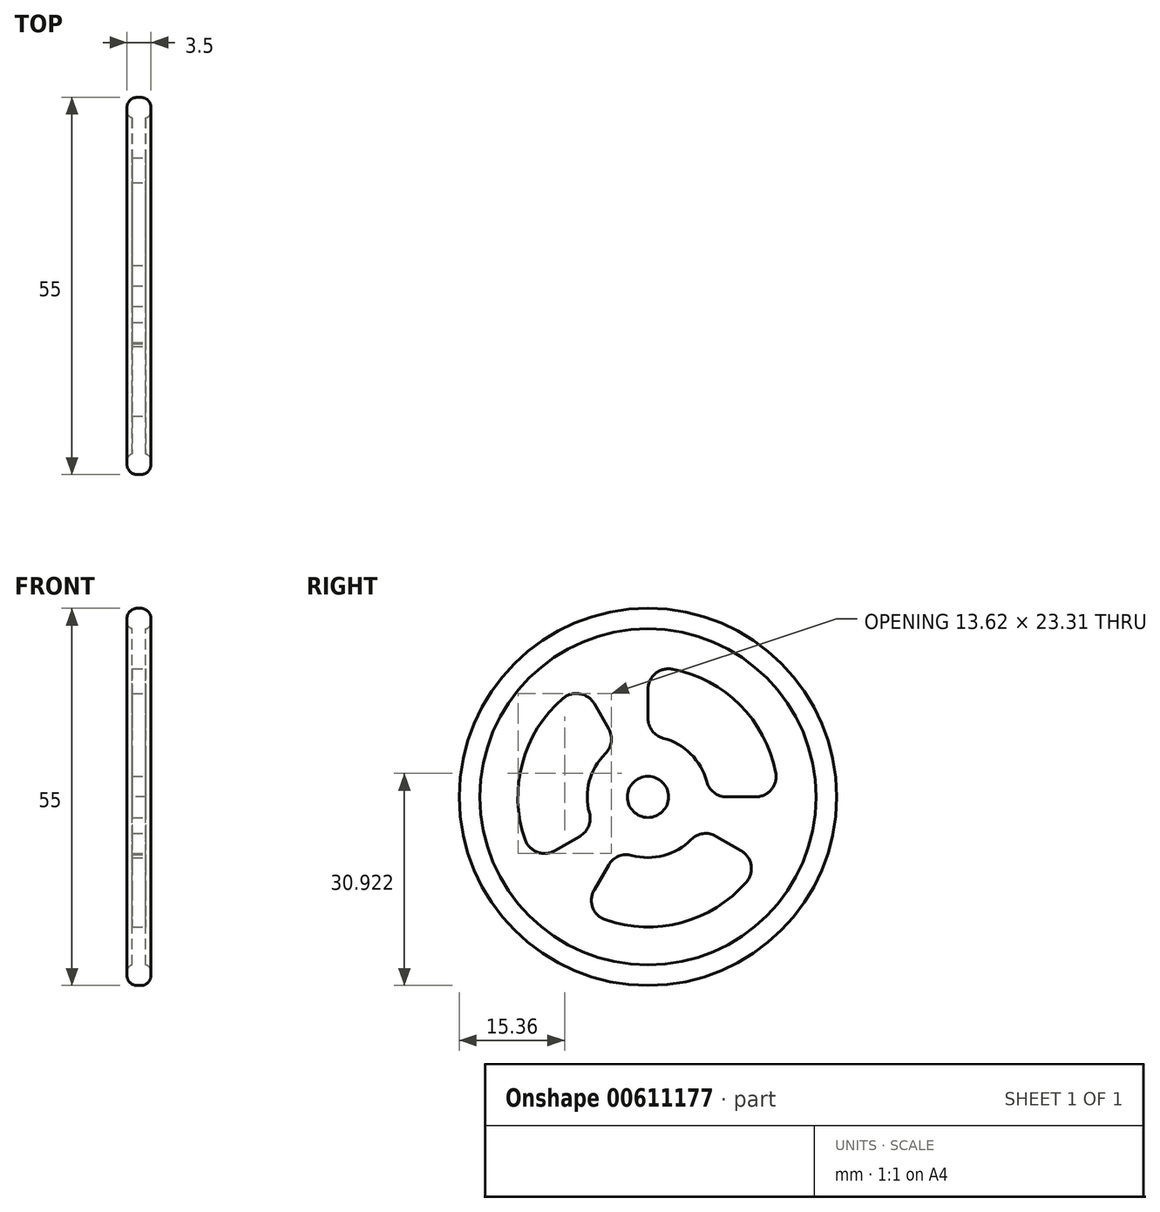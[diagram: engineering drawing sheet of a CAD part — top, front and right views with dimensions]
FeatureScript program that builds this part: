
annotation { "Feature Type Name" : "Feature", "Feature Type Description" : "" }
export const myFeature = defineFeature(function(context is Context, id is Id, definition is map)
    precondition{}
    {
        {
            var Q0;
            Q0=qCreatedBy(makeId("Right.planeOp"),FACE);
            var sketch = newSketch(context, id + "F0", { "sketchPlane" : qUnion([Q0])});
            skCircle(sketch, "E0", {"center": v(0, 0) * mm, "radius": 27.5 * mm});
            skCircle(sketch, "E1", {"center": v(0, 0) * mm, "radius": 24.5 * mm});
            skCircle(sketch, "E2", {"center": v(0, 0) * mm, "radius": 18.96 * mm});
            skCircle(sketch, "E3", {"center": v(0, 0) * mm, "radius": 8.85 * mm});
            skLineSegment(sketch, "E4", {"start": v(0, 18.96) * mm, "end": v(0, 8.85) * mm});
            skLineSegment(sketch, "E5", {"start": v(-7.66, -4.42) * mm, "end": v(-16.42, -9.48) * mm});
            skLineSegment(sketch, "E6", {"start": v(7.66, -4.42) * mm, "end": v(16.42, -9.48) * mm});
            skLineSegment(sketch, "E7", {"start": v(-4.42, 7.66) * mm, "end": v(-9.48, 16.42) * mm});
            skLineSegment(sketch, "E8.1.0", {"start": v(-4.42, -7.66) * mm, "end": v(-9.48, -16.42) * mm});
            skLineSegment(sketch, "E8.2.0", {"start": v(8.85, 0) * mm, "end": v(18.96, 0) * mm});
            skCircle(sketch, "E9", {"center": v(0, 0) * mm, "radius": 3 * mm});
            skSolve(sketch);
        }
        {
            var Q0;
            Q0=makeQuery(id+"F0.imprint","IMPRINT",FACE,{"disambiguationData":[TD([[makeQuery(id+"F0.imprint","IMPRINT",EDGE,{"derivedFrom":sQuery(id+"F0.wireOp",EDGE,"E1")}),1.0]])]});
            var Q1;
            {var subQ0=sQuery(id+"F0.wireOp",EDGE,"E3");var subQ1=makeQuery(id+"F0.imprint","INTERSECT",VERTEX,{"derivedFrom":[subQ0,sQuery(id+"F0.wireOp",EDGE,"E4")]});Q1=makeQuery(id+"F0.imprint","IMPRINT",FACE,{"disambiguationData":[TD([[makeQuery(id+"F0.imprint","IMPRINT",EDGE,{"disambiguationData":[TD([[subQ1,-1.0]])],"derivedFrom":subQ0}),1.0]])]});}
            var Q2;
            {var subQ0=sQuery(id+"F0.wireOp",EDGE,"E4");Q2=makeQuery(id+"F0.imprint","IMPRINT",FACE,{"disambiguationData":[TD([[makeQuery(id+"F0.imprint","IMPRINT",EDGE,{"derivedFrom":subQ0}),-1.0]])]});}
            var Q3;
            {var subQ0=sQuery(id+"F0.wireOp",EDGE,"E5");Q3=makeQuery(id+"F0.imprint","IMPRINT",FACE,{"disambiguationData":[TD([[makeQuery(id+"F0.imprint","IMPRINT",EDGE,{"derivedFrom":subQ0}),1.0]])]});}
            var Q4;
            {var subQ0=sQuery(id+"F0.wireOp",EDGE,"E6");Q4=makeQuery(id+"F0.imprint","IMPRINT",FACE,{"disambiguationData":[TD([[makeQuery(id+"F0.imprint","IMPRINT",EDGE,{"derivedFrom":subQ0}),1.0]])]});}
            extrude(context, id + "F1", {"entities" : qUnion([Q0, Q1, Q2, Q3, Q4]), "endBound" : BoundingType.SYMMETRIC, "oppositeDirection" : true, "depth" : 2 * mm, "offsetDistance" : 25.4 * mm});
        }
        {
            var Q0;
            Q0=qSketchRegion(id+"F0",true);
            extrude(context, id + "F2", {"entities" : qUnion([Q0]), "operationType" : NewBodyOperationType.ADD, "endBound" : BoundingType.SYMMETRIC, "depth" : 3.5 * mm, "offsetDistance" : 25.4 * mm});
        }
        {
            var Q0;
            Q0=makeQuery(id+"F2.opExtrude","CAP_EDGE",EDGE,{"disambiguationData":[OSD([sQuery(id+"F0.wireOp",EDGE,"E0")])],"isStart":true});
            var Q1;
            Q1=makeQuery(id+"F2.opExtrude","CAP_EDGE",EDGE,{"disambiguationData":[OSD([sQuery(id+"F0.wireOp",EDGE,"E0")])],"isStart":false});
            fillet(context, id + "F3", {"entities" : qUnion([Q0, Q1]), "radius" : 1.5 * mm, "tangentPropagation" : true, "allowEdgeOverflow" : false});
        }
        {
            var Q0;
            Q0=makeQuery(id+"F2.opExtrude","CAP_EDGE",EDGE,{"disambiguationData":[OSD([sQuery(id+"F0.wireOp",EDGE,"E1")])],"isStart":false});
            var Q1;
            Q1=makeQuery(id+"F2.opExtrude","CAP_EDGE",EDGE,{"disambiguationData":[OSD([sQuery(id+"F0.wireOp",EDGE,"E1")])],"isStart":true});
            fillet(context, id + "F4", {"entities" : qUnion([Q0, Q1]), "radius" : 1 * mm, "tangentPropagation" : true, "allowEdgeOverflow" : false});
        }
        {
            var Q0;
            Q0=makeQuery(id+"F1.opExtrude","SWEPT_EDGE",EDGE,{"disambiguationData":[OSD([sQuery(id+"F0.wireOp",EDGE,"E2"),sQuery(id+"F0.wireOp",EDGE,"E5")])]});
            var Q1;
            Q1=makeQuery(id+"F1.opExtrude","SWEPT_EDGE",EDGE,{"disambiguationData":[OSD([sQuery(id+"F0.wireOp",EDGE,"E3"),sQuery(id+"F0.wireOp",EDGE,"E5")])]});
            var Q2;
            Q2=makeQuery(id+"F1.opExtrude","SWEPT_EDGE",EDGE,{"disambiguationData":[OSD([sQuery(id+"F0.wireOp",EDGE,"E3"),sQuery(id+"F0.wireOp",EDGE,"E7")])]});
            var Q3;
            Q3=makeQuery(id+"F1.opExtrude","SWEPT_EDGE",EDGE,{"disambiguationData":[OSD([sQuery(id+"F0.wireOp",EDGE,"E2"),sQuery(id+"F0.wireOp",EDGE,"E4")])]});
            var Q4;
            Q4=makeQuery(id+"F1.opExtrude","SWEPT_EDGE",EDGE,{"disambiguationData":[OSD([sQuery(id+"F0.wireOp",EDGE,"E2"),sQuery(id+"F0.wireOp",EDGE,"E7")])]});
            var Q5;
            Q5=makeQuery(id+"F1.opExtrude","SWEPT_EDGE",EDGE,{"disambiguationData":[OSD([sQuery(id+"F0.wireOp",EDGE,"E3"),sQuery(id+"F0.wireOp",EDGE,"E8.1.0")])]});
            var Q6;
            Q6=makeQuery(id+"F1.opExtrude","SWEPT_EDGE",EDGE,{"disambiguationData":[OSD([sQuery(id+"F0.wireOp",EDGE,"E3"),sQuery(id+"F0.wireOp",EDGE,"E6")])]});
            var Q7;
            Q7=makeQuery(id+"F1.opExtrude","SWEPT_EDGE",EDGE,{"disambiguationData":[OSD([sQuery(id+"F0.wireOp",EDGE,"E3"),sQuery(id+"F0.wireOp",EDGE,"E4")])]});
            var Q8;
            Q8=makeQuery(id+"F1.opExtrude","SWEPT_EDGE",EDGE,{"disambiguationData":[OSD([sQuery(id+"F0.wireOp",EDGE,"E3"),sQuery(id+"F0.wireOp",EDGE,"E8.2.0")])]});
            var Q9;
            Q9=makeQuery(id+"F1.opExtrude","SWEPT_EDGE",EDGE,{"disambiguationData":[OSD([sQuery(id+"F0.wireOp",EDGE,"E2"),sQuery(id+"F0.wireOp",EDGE,"E8.1.0")])]});
            var Q10;
            Q10=makeQuery(id+"F1.opExtrude","SWEPT_EDGE",EDGE,{"disambiguationData":[OSD([sQuery(id+"F0.wireOp",EDGE,"E2"),sQuery(id+"F0.wireOp",EDGE,"E6")])]});
            var Q11;
            Q11=makeQuery(id+"F1.opExtrude","SWEPT_EDGE",EDGE,{"disambiguationData":[OSD([sQuery(id+"F0.wireOp",EDGE,"E2"),sQuery(id+"F0.wireOp",EDGE,"E8.2.0")])]});
            fillet(context, id + "F5", {"entities" : qUnion([Q0, Q1, Q2, Q3, Q4, Q5, Q6, Q7, Q8, Q9, Q10, Q11]), "radius" : 3 * mm, "tangentPropagation" : true, "allowEdgeOverflow" : false});
        }
    });
